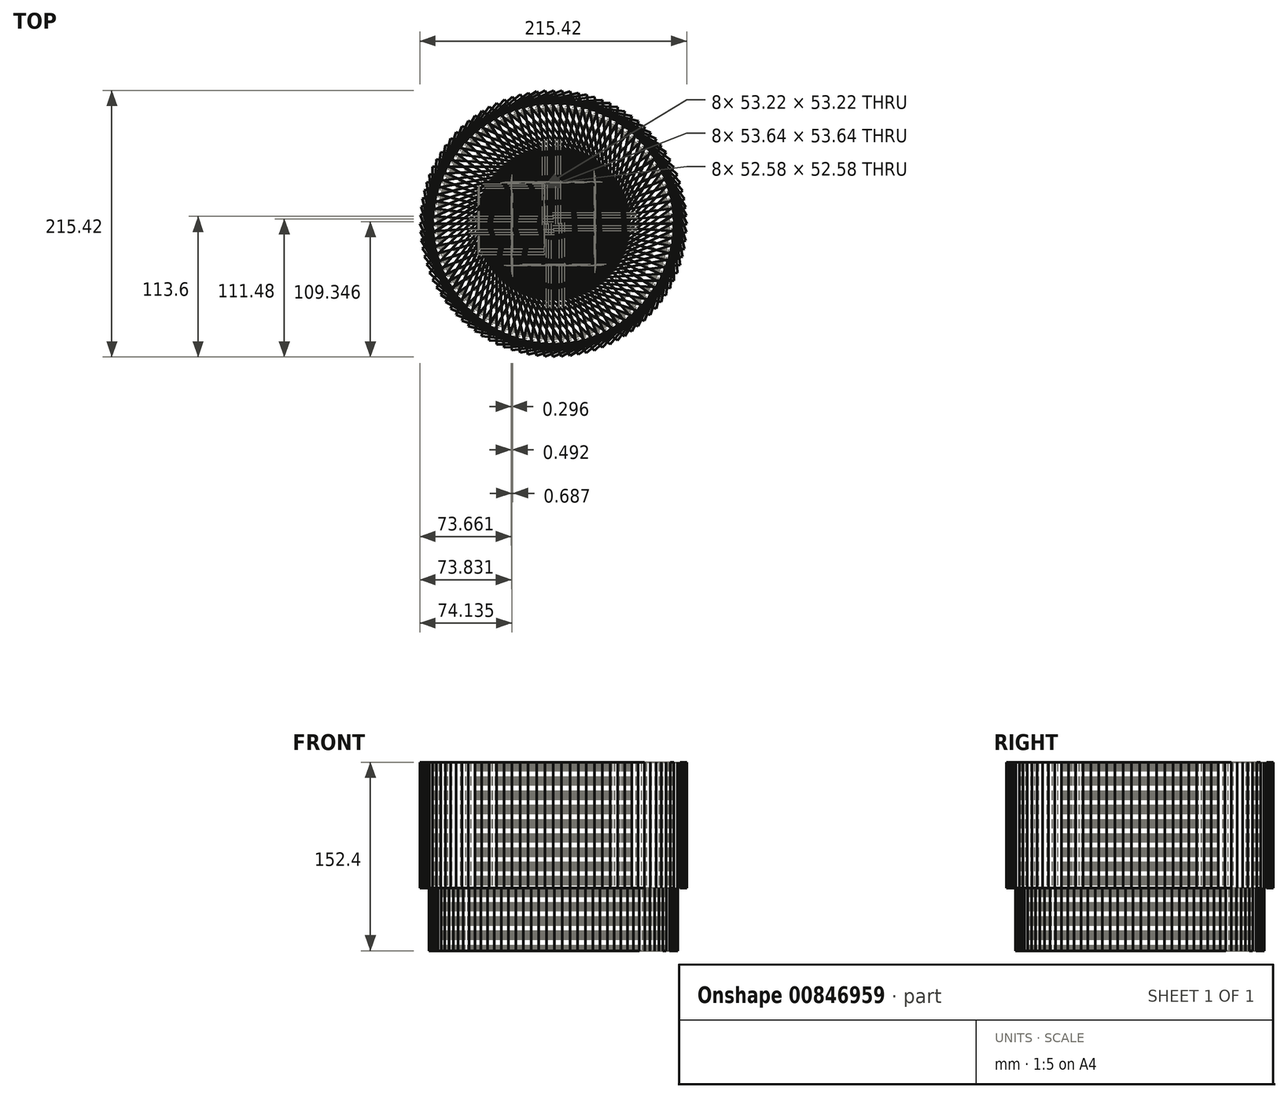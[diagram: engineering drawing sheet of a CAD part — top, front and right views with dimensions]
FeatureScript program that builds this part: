
annotation { "Feature Type Name" : "Feature", "Feature Type Description" : "" }
export const myFeature = defineFeature(function(context is Context, id is Id, definition is map)
    precondition{}
    {
        {
            var Q0;
            Q0=qCreatedBy(makeId("Top.planeOp"),FACE);
            var sketch = newSketch(context, id + "F0", { "sketchPlane" : qUnion([Q0])});
            skLineSegment(sketch, "E0.bottom", {"start": v(-5.84, 25.71) * mm, "end": v(-43.94, 25.71) * mm});
            skLineSegment(sketch, "E0.top", {"start": v(-5.84, -12.39) * mm, "end": v(-43.94, -12.39) * mm});
            skLineSegment(sketch, "E0.left", {"start": v(-5.84, 25.71) * mm, "end": v(-5.84, -12.39) * mm});
            skLineSegment(sketch, "E0.right", {"start": v(-43.94, 25.71) * mm, "end": v(-43.94, -12.39) * mm});
            skLineSegment(sketch, "E1.bottom", {"start": v(3.1, 25.71) * mm, "end": v(41.2, 25.71) * mm});
            skLineSegment(sketch, "E1.top", {"start": v(3.1, -12.39) * mm, "end": v(41.2, -12.39) * mm});
            skLineSegment(sketch, "E1.left", {"start": v(3.1, 25.71) * mm, "end": v(3.1, -12.39) * mm});
            skLineSegment(sketch, "E1.right", {"start": v(41.2, 25.71) * mm, "end": v(41.2, -12.39) * mm});
            skLineSegment(sketch, "E2", {"start": v(-5.84, 25.71) * mm, "end": v(3.1, 25.71) * mm});
            skLineSegment(sketch, "E3", {"start": v(3.1, -12.39) * mm, "end": v(-5.84, -12.39) * mm});
            skSolve(sketch);
        }
        {
            var Q0;
            Q0=makeQuery(id+"F0.imprint","IMPRINT",FACE,{"disambiguationData":[TD([[makeQuery(id+"F0.imprint","IMPRINT",EDGE,{"derivedFrom":sQuery(id+"F0.wireOp",EDGE,"E0.bottom")}),1.0]])]});
            var Q1;
            Q1=makeQuery(id+"F0.imprint","IMPRINT",FACE,{"disambiguationData":[TD([[makeQuery(id+"F0.imprint","IMPRINT",EDGE,{"derivedFrom":sQuery(id+"F0.wireOp",EDGE,"E1.bottom")}),-1.0]])]});
            extrude(context, id + "F1", {"entities" : qUnion([Q0, Q1]), "depth" : 25.4 * mm, "offsetDistance" : 25.4 * mm, "hasSecondDirection" : true, "secondDirectionOppositeDirection" : true, "secondDirectionDepth" : 25.4 * mm});
        }
        {
            var Q0;
            Q0=makeQuery(id+"F1.opExtrude","CAP_FACE",FACE,{"disambiguationData":[OSD([sQuery(id+"F0.wireOp",EDGE,"E0.bottom"),sQuery(id+"F0.wireOp",EDGE,"E0.top"),sQuery(id+"F0.wireOp",EDGE,"E0.left"),sQuery(id+"F0.wireOp",EDGE,"E0.right")])],"isStart":false});
            var sketch = newSketch(context, id + "F2", { "sketchPlane" : qUnion([Q0])});
            skLineSegment(sketch, "E4.bottom", {"start": v(-50.08, 29.63) * mm, "end": v(47.35, 29.63) * mm});
            skLineSegment(sketch, "E4.top", {"start": v(-50.08, -16.3) * mm, "end": v(47.35, -16.3) * mm});
            skLineSegment(sketch, "E4.left", {"start": v(-50.08, 29.63) * mm, "end": v(-50.08, -16.3) * mm});
            skLineSegment(sketch, "E4.right", {"start": v(47.35, 29.63) * mm, "end": v(47.35, -16.3) * mm});
            skSolve(sketch);
        }
        {
            var Q0;
            Q0=makeQuery(id+"F2.imprint","IMPRINT",FACE,{"disambiguationData":[TD([[makeQuery(id+"F2.imprint","IMPRINT",EDGE,{"derivedFrom":sQuery(id+"F2.wireOp",EDGE,"E4.bottom")}),-1.0]])]});
            extrude(context, id + "F3", {"entities" : qUnion([Q0]), "operationType" : NewBodyOperationType.ADD, "depth" : 101.6 * mm, "offsetDistance" : 25.4 * mm});
        }
        {
            var Q0;
            Q0=makeQuery(id+"F1.opExtrude","SWEPT_BODY",BODY,{"disambiguationData":[OSD([sQuery(id+"F0.wireOp",EDGE,"E0.bottom"),sQuery(id+"F0.wireOp",EDGE,"E0.top"),sQuery(id+"F0.wireOp",EDGE,"E0.left"),sQuery(id+"F0.wireOp",EDGE,"E0.right")])]});
            var Q1;
            Q1=makeQuery(id+"F1.opExtrude","SWEPT_BODY",BODY,{"disambiguationData":[OSD([sQuery(id+"F0.wireOp",EDGE,"E1.bottom"),sQuery(id+"F0.wireOp",EDGE,"E1.top"),sQuery(id+"F0.wireOp",EDGE,"E1.left"),sQuery(id+"F0.wireOp",EDGE,"E1.right")])]});
            var Q2;
            Q2=makeQuery(id+"F3.opExtrude","SWEPT_EDGE",EDGE,{"disambiguationData":[OSD([sQuery(id+"F2.wireOp",EDGE,"E4.bottom"),sQuery(id+"F2.wireOp",EDGE,"E4.left")])]});
            circularPattern(context, id + "F4", {"entities" : qUnion([Q0, Q1]), "axis" : qUnion([Q2]), "angle" : 360 * degree, "instanceCount" : 100, "equalSpace" : true});
        }
    });
